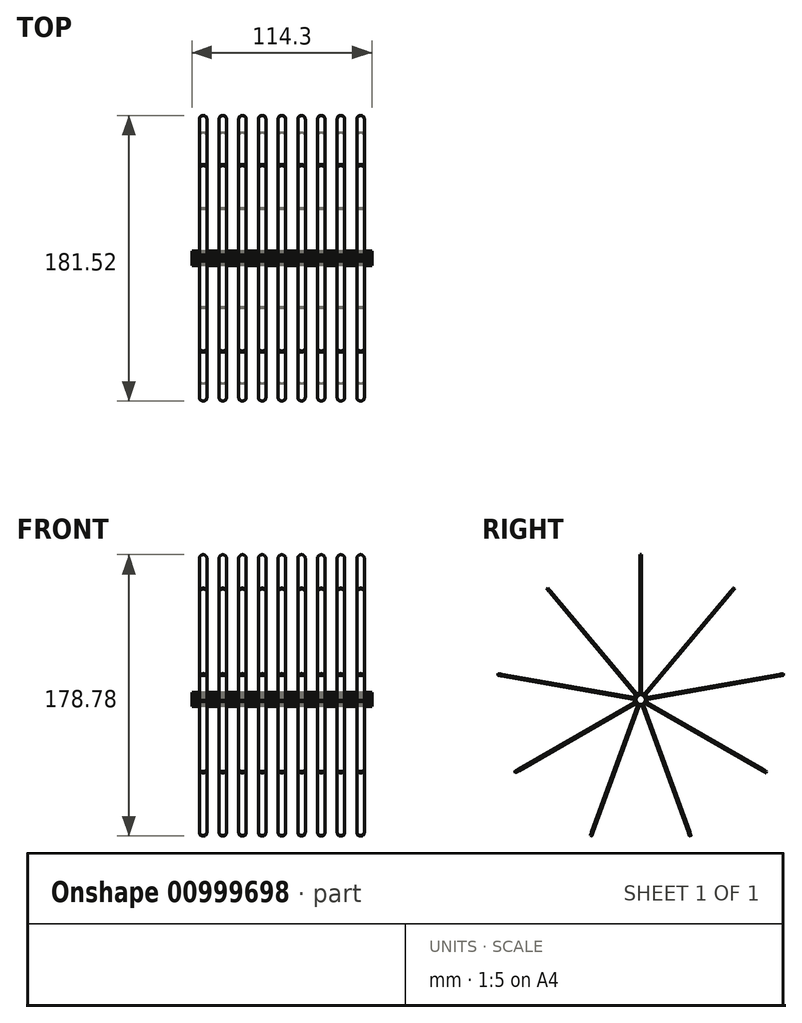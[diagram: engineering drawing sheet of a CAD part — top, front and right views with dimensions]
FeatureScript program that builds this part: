
annotation { "Feature Type Name" : "Feature", "Feature Type Description" : "" }
export const myFeature = defineFeature(function(context is Context, id is Id, definition is map)
    precondition{}
    {
        {
            var Q0;
            Q0=qCreatedBy(makeId("Right.planeOp"),FACE);
            var sketch = newSketch(context, id + "F0", { "sketchPlane" : qUnion([Q0])});
            skLineSegment(sketch, "E0.bottom", {"start": v(-3.17, -3.17) * mm, "end": v(3.18, -3.17) * mm});
            skLineSegment(sketch, "E0.top", {"start": v(-3.18, 3.17) * mm, "end": v(3.17, 3.17) * mm});
            skLineSegment(sketch, "E0.left", {"start": v(-3.17, -3.17) * mm, "end": v(-3.18, 3.17) * mm});
            skLineSegment(sketch, "E0.right", {"start": v(3.18, -3.17) * mm, "end": v(3.17, 3.18) * mm});
            skPoint(sketch, "E0.middle", {"position": v(0, 0) * mm});
            skSolve(sketch);
        }
        {
            var Q0;
            Q0=makeQuery(id+"F0.imprint","IMPRINT",FACE,{"disambiguationData":[TD([[makeQuery(id+"F0.imprint","IMPRINT",EDGE,{"derivedFrom":sQuery(id+"F0.wireOp",EDGE,"E0.bottom")}),1.0]])]});
            extrude(context, id + "F1", {"entities" : qUnion([Q0]), "depth" : 114.3 * mm, "offsetDistance" : 25.4 * mm});
        }
        {
            var Q0;
            Q0=qCreatedBy(makeId("Front.planeOp"),FACE);
            var sketch = newSketch(context, id + "F2", { "sketchPlane" : qUnion([Q0])});
            skLineSegment(sketch, "E1", {"start": v(4.76, 3.17) * mm, "end": v(4.76, 89.7) * mm});
            skArc(sketch, "E2", {"start": v(9.52, 89.7) * mm, "mid": v(7.14, 92.08) * mm, "end": v(4.76, 89.7) * mm});
            skLineSegment(sketch, "E3", {"start": v(9.52, 89.7) * mm, "end": v(9.53, 3.17) * mm});
            skLineSegment(sketch, "E4", {"start": v(9.53, 3.17) * mm, "end": v(4.76, 3.17) * mm});
            skLineSegment(sketch, "E5.1.0.0", {"start": v(17.26, 3.17) * mm, "end": v(17.26, 89.7) * mm});
            skArc(sketch, "E5.1.0.1", {"start": v(22.03, 89.7) * mm, "mid": v(19.65, 92.08) * mm, "end": v(17.26, 89.7) * mm});
            skLineSegment(sketch, "E5.1.0.2", {"start": v(22.03, 89.7) * mm, "end": v(22.03, 3.17) * mm});
            skLineSegment(sketch, "E5.1.0.3", {"start": v(22.03, 3.17) * mm, "end": v(17.26, 3.17) * mm});
            skLineSegment(sketch, "E5.2.0.0", {"start": v(29.77, 3.17) * mm, "end": v(29.77, 89.7) * mm});
            skArc(sketch, "E5.2.0.1", {"start": v(34.53, 89.7) * mm, "mid": v(32.15, 92.08) * mm, "end": v(29.77, 89.7) * mm});
            skLineSegment(sketch, "E5.2.0.2", {"start": v(34.53, 89.7) * mm, "end": v(34.53, 3.17) * mm});
            skLineSegment(sketch, "E5.2.0.3", {"start": v(34.53, 3.17) * mm, "end": v(29.77, 3.17) * mm});
            skLineSegment(sketch, "E5.3.0.0", {"start": v(42.27, 3.17) * mm, "end": v(42.27, 89.7) * mm});
            skArc(sketch, "E5.3.0.1", {"start": v(47.03, 89.7) * mm, "mid": v(44.65, 92.08) * mm, "end": v(42.27, 89.7) * mm});
            skLineSegment(sketch, "E5.3.0.2", {"start": v(47.03, 89.7) * mm, "end": v(47.03, 3.17) * mm});
            skLineSegment(sketch, "E5.3.0.3", {"start": v(47.03, 3.17) * mm, "end": v(42.27, 3.17) * mm});
            skLineSegment(sketch, "E5.4.0.0", {"start": v(54.77, 3.17) * mm, "end": v(54.77, 89.7) * mm});
            skArc(sketch, "E5.4.0.1", {"start": v(59.53, 89.7) * mm, "mid": v(57.15, 92.08) * mm, "end": v(54.77, 89.7) * mm});
            skLineSegment(sketch, "E5.4.0.2", {"start": v(59.53, 89.7) * mm, "end": v(59.53, 3.17) * mm});
            skLineSegment(sketch, "E5.4.0.3", {"start": v(59.53, 3.17) * mm, "end": v(54.77, 3.17) * mm});
            skLineSegment(sketch, "E5.5.0.0", {"start": v(67.27, 3.17) * mm, "end": v(67.27, 89.7) * mm});
            skArc(sketch, "E5.5.0.1", {"start": v(72.03, 89.7) * mm, "mid": v(69.65, 92.08) * mm, "end": v(67.27, 89.7) * mm});
            skLineSegment(sketch, "E5.5.0.2", {"start": v(72.03, 89.7) * mm, "end": v(72.03, 3.17) * mm});
            skLineSegment(sketch, "E5.5.0.3", {"start": v(72.03, 3.17) * mm, "end": v(67.27, 3.17) * mm});
            skLineSegment(sketch, "E5.6.0.0", {"start": v(79.77, 3.17) * mm, "end": v(79.77, 89.7) * mm});
            skArc(sketch, "E5.6.0.1", {"start": v(84.53, 89.7) * mm, "mid": v(82.15, 92.08) * mm, "end": v(79.77, 89.7) * mm});
            skLineSegment(sketch, "E5.6.0.2", {"start": v(84.53, 89.7) * mm, "end": v(84.53, 3.17) * mm});
            skLineSegment(sketch, "E5.6.0.3", {"start": v(84.53, 3.17) * mm, "end": v(79.77, 3.17) * mm});
            skLineSegment(sketch, "E5.7.0.0", {"start": v(92.27, 3.17) * mm, "end": v(92.27, 89.7) * mm});
            skArc(sketch, "E5.7.0.1", {"start": v(97.04, 89.7) * mm, "mid": v(94.65, 92.08) * mm, "end": v(92.27, 89.7) * mm});
            skLineSegment(sketch, "E5.7.0.2", {"start": v(97.04, 89.7) * mm, "end": v(97.04, 3.17) * mm});
            skLineSegment(sketch, "E5.7.0.3", {"start": v(97.04, 3.17) * mm, "end": v(92.27, 3.17) * mm});
            skLineSegment(sketch, "E5.8.0.0", {"start": v(104.78, 3.17) * mm, "end": v(104.78, 89.7) * mm});
            skArc(sketch, "E5.8.0.1", {"start": v(109.54, 89.7) * mm, "mid": v(107.16, 92.08) * mm, "end": v(104.78, 89.7) * mm});
            skLineSegment(sketch, "E5.8.0.2", {"start": v(109.54, 89.7) * mm, "end": v(109.54, 3.17) * mm});
            skLineSegment(sketch, "E5.8.0.3", {"start": v(109.54, 3.17) * mm, "end": v(104.78, 3.17) * mm});
            skLineSegment(sketch, "E5.direction1", {"start": v(4.76, 3.17) * mm, "end": v(17.26, 3.17) * mm, "construction": true});
            skSolve(sketch);
        }
        {
            var Q0;
            Q0 = qSketchRegion(id + "F2", true);
            extrude(context, id + "F3", {"entities" : qUnion([Q0]), "operationType" : NewBodyOperationType.ADD, "depth" : 0.5 * mm, "offsetDistance" : 25.4 * mm, "hasSecondDirection" : true, "secondDirectionOppositeDirection" : true, "secondDirectionDepth" : 0.5 * mm});
        }
        {
            var Q0;
            Q0=qCreatedBy(makeId("Front.planeOp"),FACE);
            var sketch = newSketch(context, id + "F4", { "sketchPlane" : qUnion([Q0])});
            skLineSegment(sketch, "E6", {"start": v(0, 0) * mm, "end": v(114.3, 0) * mm});
            skSolve(sketch);
        }
        {
            var Q0;
            Q0=makeQuery(id+"F1.opExtrude","SWEPT_BODY",BODY,{"disambiguationData":[OSD([sQuery(id+"F0.wireOp",EDGE,"E0.bottom"),sQuery(id+"F0.wireOp",EDGE,"E0.top"),sQuery(id+"F0.wireOp",EDGE,"E0.left"),sQuery(id+"F0.wireOp",EDGE,"E0.right")])]});
            var Q1;
            Q1=sQuery(id+"F4.wireOp",EDGE,"E6");
            circularPattern(context, id + "F5", {"entities" : qUnion([Q0]), "axis" : qUnion([Q1]), "angle" : 360 * degree, "instanceCount" : 9, "equalSpace" : true});
        }
    });
